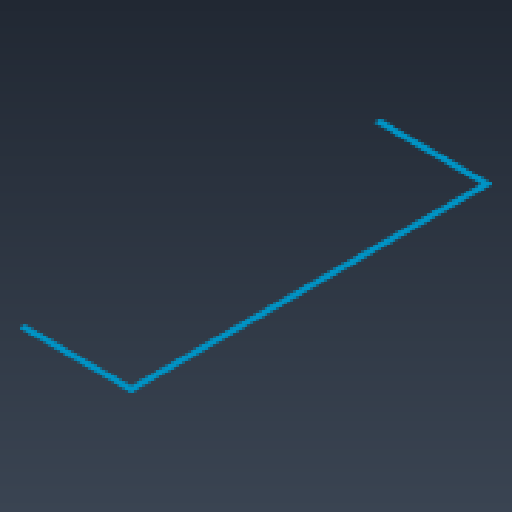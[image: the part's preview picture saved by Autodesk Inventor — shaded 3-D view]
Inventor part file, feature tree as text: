
AUTODESK INVENTOR PART (.ipt)
format: ipt  version: 2024.3 (Build 283343000, 343)  size: 83,968 bytes
history: native  units: in
note: dims shown in document units (in); Inventor stores cm internally (conversion verified against a paired STEP export)
features: extrude x1
ambient origin geometry x8: Origin, YZ Plane, XZ Plane, XY Plane, X Axis, Y Axis, Z Axis, Center Point
bodies: Solid1 (feature_tree)
feature tree (1):
  extrude  "Extrude-Thin1"  [1 undecoded]
note: 1 required parameter value undecoded (feature->parameter linkage not recoverable at this tier; creation-order binding heuristic only, values carry confidence <= 0.55)
